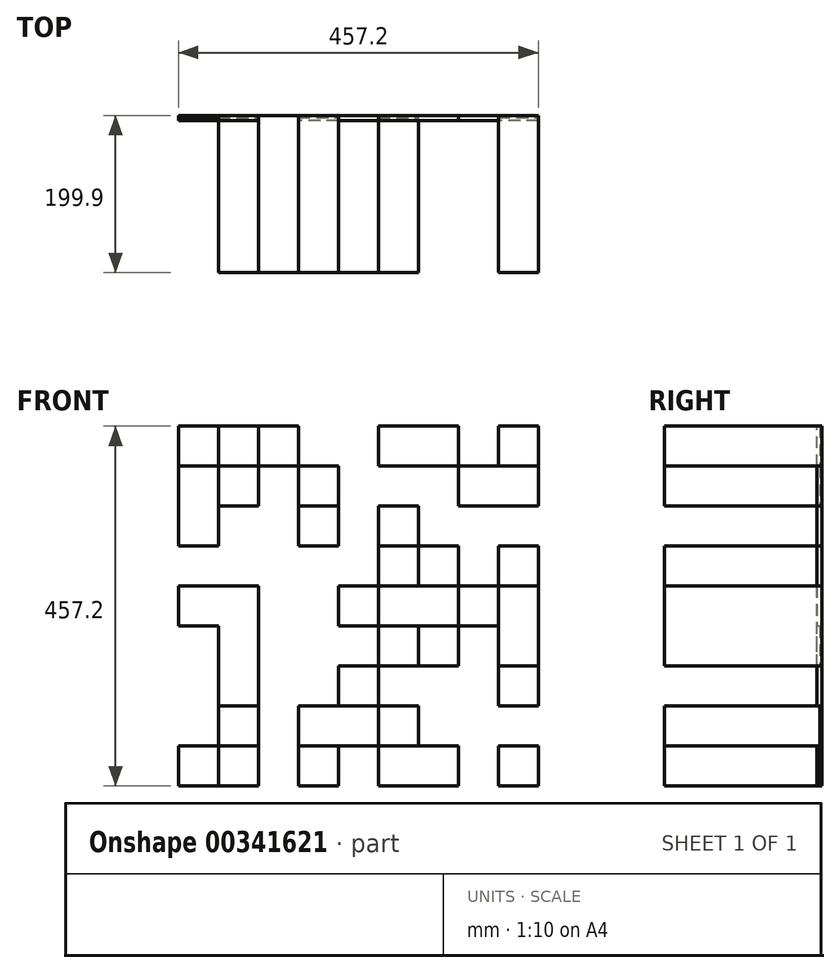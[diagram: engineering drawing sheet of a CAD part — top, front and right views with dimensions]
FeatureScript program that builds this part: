
annotation { "Feature Type Name" : "Feature", "Feature Type Description" : "" }
export const myFeature = defineFeature(function(context is Context, id is Id, definition is map)
    precondition{}
    {
        {
            var Q0;
            Q0=qCreatedBy(makeId("Front.planeOp"),FACE);
            var sketch = newSketch(context, id + "F0", { "sketchPlane" : qUnion([Q0])});
            skLineSegment(sketch, "E0.bottom", {"start": v(0, 0) * mm, "end": v(457.2, 0) * mm});
            skLineSegment(sketch, "E0.top", {"start": v(0, -457.2) * mm, "end": v(457.2, -457.2) * mm});
            skLineSegment(sketch, "E0.left", {"start": v(0, 0) * mm, "end": v(0, -457.2) * mm});
            skLineSegment(sketch, "E0.right", {"start": v(457.2, 0) * mm, "end": v(457.2, -457.2) * mm});
            skSolve(sketch);
        }
        {
            var Q0;
            Q0=qCreatedBy(makeId("Front.planeOp"),FACE);
            var sketch = newSketch(context, id + "F1", { "sketchPlane" : qUnion([Q0])});
            skLineSegment(sketch, "E1.bottom", {"start": v(0, 0) * mm, "end": v(50.8, 0) * mm});
            skLineSegment(sketch, "E1.top", {"start": v(0, -50.8) * mm, "end": v(50.8, -50.8) * mm});
            skLineSegment(sketch, "E1.left", {"start": v(0, 0) * mm, "end": v(0, -50.8) * mm});
            skLineSegment(sketch, "E1.right", {"start": v(50.8, 0) * mm, "end": v(50.8, -50.8) * mm});
            skLineSegment(sketch, "E2.bottom", {"start": v(50.8, 0) * mm, "end": v(101.6, 0) * mm});
            skLineSegment(sketch, "E2.top", {"start": v(50.8, -50.8) * mm, "end": v(101.6, -50.8) * mm});
            skLineSegment(sketch, "E2.right", {"start": v(101.6, 0) * mm, "end": v(101.6, -50.8) * mm});
            skLineSegment(sketch, "E3.bottom", {"start": v(101.6, 0) * mm, "end": v(152.4, 0) * mm});
            skLineSegment(sketch, "E3.top", {"start": v(101.6, -50.8) * mm, "end": v(152.4, -50.8) * mm});
            skLineSegment(sketch, "E3.right", {"start": v(152.4, 0) * mm, "end": v(152.4, -50.8) * mm});
            skLineSegment(sketch, "E4.bottom", {"start": v(152.4, 0) * mm, "end": v(203.2, 0) * mm});
            skLineSegment(sketch, "E4.top", {"start": v(152.4, -50.8) * mm, "end": v(203.2, -50.8) * mm});
            skLineSegment(sketch, "E4.right", {"start": v(203.2, 0) * mm, "end": v(203.2, -50.8) * mm});
            skLineSegment(sketch, "E5.bottom", {"start": v(203.2, 0) * mm, "end": v(254, 0) * mm});
            skLineSegment(sketch, "E5.top", {"start": v(203.2, -50.8) * mm, "end": v(254, -50.8) * mm});
            skLineSegment(sketch, "E5.right", {"start": v(254, 0) * mm, "end": v(254, -50.8) * mm});
            skLineSegment(sketch, "E6.bottom", {"start": v(254, 0) * mm, "end": v(304.8, 0) * mm});
            skLineSegment(sketch, "E6.top", {"start": v(254, -50.8) * mm, "end": v(304.8, -50.8) * mm});
            skLineSegment(sketch, "E6.right", {"start": v(304.8, 0) * mm, "end": v(304.8, -50.8) * mm});
            skLineSegment(sketch, "E7.bottom", {"start": v(304.8, 0) * mm, "end": v(355.6, 0) * mm});
            skLineSegment(sketch, "E7.top", {"start": v(304.8, -50.8) * mm, "end": v(355.6, -50.8) * mm});
            skLineSegment(sketch, "E7.right", {"start": v(355.6, 0) * mm, "end": v(355.6, -50.8) * mm});
            skLineSegment(sketch, "E8.bottom", {"start": v(355.6, 0) * mm, "end": v(406.4, 0) * mm});
            skLineSegment(sketch, "E8.top", {"start": v(355.6, -50.8) * mm, "end": v(406.4, -50.8) * mm});
            skLineSegment(sketch, "E8.right", {"start": v(406.4, 0) * mm, "end": v(406.4, -50.8) * mm});
            skLineSegment(sketch, "E9.bottom", {"start": v(406.4, 0) * mm, "end": v(457.2, 0) * mm});
            skLineSegment(sketch, "E9.top", {"start": v(406.4, -50.8) * mm, "end": v(457.2, -50.8) * mm});
            skLineSegment(sketch, "E9.right", {"start": v(457.2, 0) * mm, "end": v(457.2, -50.8) * mm});
            skLineSegment(sketch, "E10.top", {"start": v(0, -101.6) * mm, "end": v(50.8, -101.6) * mm});
            skLineSegment(sketch, "E10.left", {"start": v(0, -50.8) * mm, "end": v(0, -101.6) * mm});
            skLineSegment(sketch, "E10.right", {"start": v(50.8, -50.8) * mm, "end": v(50.8, -101.6) * mm});
            skLineSegment(sketch, "E11.top", {"start": v(50.8, -101.6) * mm, "end": v(101.6, -101.6) * mm});
            skLineSegment(sketch, "E11.right", {"start": v(101.6, -50.8) * mm, "end": v(101.6, -101.6) * mm});
            skLineSegment(sketch, "E12.top", {"start": v(50.8, -152.4) * mm, "end": v(101.6, -152.4) * mm});
            skLineSegment(sketch, "E12.left", {"start": v(50.8, -101.6) * mm, "end": v(50.8, -152.4) * mm});
            skLineSegment(sketch, "E12.right", {"start": v(101.6, -101.6) * mm, "end": v(101.6, -152.4) * mm});
            skLineSegment(sketch, "E13.bottom", {"start": v(101.6, -101.6) * mm, "end": v(152.4, -101.6) * mm});
            skLineSegment(sketch, "E13.top", {"start": v(101.6, -152.4) * mm, "end": v(152.4, -152.4) * mm});
            skLineSegment(sketch, "E13.right", {"start": v(152.4, -101.6) * mm, "end": v(152.4, -152.4) * mm});
            skLineSegment(sketch, "E14.top", {"start": v(304.8, -101.6) * mm, "end": v(355.6, -101.6) * mm});
            skLineSegment(sketch, "E14.left", {"start": v(304.8, -50.8) * mm, "end": v(304.8, -101.6) * mm});
            skLineSegment(sketch, "E14.right", {"start": v(355.6, -50.8) * mm, "end": v(355.6, -101.6) * mm});
            skLineSegment(sketch, "E15.top", {"start": v(0, -152.4) * mm, "end": v(50.8, -152.4) * mm});
            skLineSegment(sketch, "E15.left", {"start": v(0, -101.6) * mm, "end": v(0, -152.4) * mm});
            skLineSegment(sketch, "E16.top", {"start": v(406.4, -101.6) * mm, "end": v(457.2, -101.6) * mm});
            skLineSegment(sketch, "E16.left", {"start": v(406.4, -50.8) * mm, "end": v(406.4, -101.6) * mm});
            skLineSegment(sketch, "E16.right", {"start": v(457.2, -50.8) * mm, "end": v(457.2, -101.6) * mm});
            skLineSegment(sketch, "E17.top", {"start": v(355.6, -101.6) * mm, "end": v(406.4, -101.6) * mm});
            skLineSegment(sketch, "E18.top", {"start": v(254, -101.6) * mm, "end": v(304.8, -101.6) * mm});
            skLineSegment(sketch, "E18.left", {"start": v(254, -50.8) * mm, "end": v(254, -101.6) * mm});
            skLineSegment(sketch, "E19.top", {"start": v(152.4, -101.6) * mm, "end": v(203.2, -101.6) * mm});
            skLineSegment(sketch, "E19.left", {"start": v(152.4, -50.8) * mm, "end": v(152.4, -101.6) * mm});
            skLineSegment(sketch, "E19.right", {"start": v(203.2, -50.8) * mm, "end": v(203.2, -101.6) * mm});
            skLineSegment(sketch, "E20.top", {"start": v(203.2, -101.6) * mm, "end": v(254, -101.6) * mm});
            skLineSegment(sketch, "E21.top", {"start": v(0, -203.2) * mm, "end": v(50.8, -203.2) * mm});
            skLineSegment(sketch, "E21.left", {"start": v(0, -152.4) * mm, "end": v(0, -203.2) * mm});
            skLineSegment(sketch, "E21.right", {"start": v(50.8, -152.4) * mm, "end": v(50.8, -203.2) * mm});
            skLineSegment(sketch, "E22.top", {"start": v(50.8, -203.2) * mm, "end": v(101.6, -203.2) * mm});
            skLineSegment(sketch, "E22.right", {"start": v(101.6, -152.4) * mm, "end": v(101.6, -203.2) * mm});
            skLineSegment(sketch, "E23.bottom", {"start": v(152.4, -152.4) * mm, "end": v(203.2, -152.4) * mm});
            skLineSegment(sketch, "E23.top", {"start": v(152.4, -203.2) * mm, "end": v(203.2, -203.2) * mm});
            skLineSegment(sketch, "E23.left", {"start": v(152.4, -152.4) * mm, "end": v(152.4, -203.2) * mm});
            skLineSegment(sketch, "E23.right", {"start": v(203.2, -152.4) * mm, "end": v(203.2, -203.2) * mm});
            skLineSegment(sketch, "E24.top", {"start": v(304.8, -152.4) * mm, "end": v(355.6, -152.4) * mm});
            skLineSegment(sketch, "E24.left", {"start": v(304.8, -101.6) * mm, "end": v(304.8, -152.4) * mm});
            skLineSegment(sketch, "E24.right", {"start": v(355.6, -101.6) * mm, "end": v(355.6, -152.4) * mm});
            skLineSegment(sketch, "E25.top", {"start": v(406.4, -152.4) * mm, "end": v(457.2, -152.4) * mm});
            skLineSegment(sketch, "E25.left", {"start": v(406.4, -101.6) * mm, "end": v(406.4, -152.4) * mm});
            skLineSegment(sketch, "E25.right", {"start": v(457.2, -101.6) * mm, "end": v(457.2, -152.4) * mm});
            skLineSegment(sketch, "E26.top", {"start": v(101.6, -203.2) * mm, "end": v(152.4, -203.2) * mm});
            skLineSegment(sketch, "E27.bottom", {"start": v(203.2, -152.4) * mm, "end": v(254, -152.4) * mm});
            skLineSegment(sketch, "E27.top", {"start": v(203.2, -203.2) * mm, "end": v(254, -203.2) * mm});
            skLineSegment(sketch, "E27.right", {"start": v(254, -152.4) * mm, "end": v(254, -203.2) * mm});
            skLineSegment(sketch, "E28.bottom", {"start": v(254, -152.4) * mm, "end": v(304.8, -152.4) * mm});
            skLineSegment(sketch, "E28.top", {"start": v(254, -203.2) * mm, "end": v(304.8, -203.2) * mm});
            skLineSegment(sketch, "E28.right", {"start": v(304.8, -152.4) * mm, "end": v(304.8, -203.2) * mm});
            skLineSegment(sketch, "E29.left", {"start": v(254, -101.6) * mm, "end": v(254, -152.4) * mm});
            skLineSegment(sketch, "E30.top", {"start": v(355.6, -152.4) * mm, "end": v(406.4, -152.4) * mm});
            skLineSegment(sketch, "E31.left", {"start": v(203.2, -101.6) * mm, "end": v(203.2, -152.4) * mm});
            skLineSegment(sketch, "E32.bottom", {"start": v(304.8, -203.2) * mm, "end": v(355.6, -203.2) * mm});
            skLineSegment(sketch, "E32.top", {"start": v(304.8, -254) * mm, "end": v(355.6, -254) * mm});
            skLineSegment(sketch, "E32.left", {"start": v(304.8, -203.2) * mm, "end": v(304.8, -254) * mm});
            skLineSegment(sketch, "E32.right", {"start": v(355.6, -203.2) * mm, "end": v(355.6, -254) * mm});
            skLineSegment(sketch, "E33.top", {"start": v(203.2, -254) * mm, "end": v(254, -254) * mm});
            skLineSegment(sketch, "E33.left", {"start": v(203.2, -203.2) * mm, "end": v(203.2, -254) * mm});
            skLineSegment(sketch, "E33.right", {"start": v(254, -203.2) * mm, "end": v(254, -254) * mm});
            skLineSegment(sketch, "E34.bottom", {"start": v(355.6, -203.2) * mm, "end": v(406.4, -203.2) * mm});
            skLineSegment(sketch, "E34.top", {"start": v(355.6, -254) * mm, "end": v(406.4, -254) * mm});
            skLineSegment(sketch, "E34.right", {"start": v(406.4, -203.2) * mm, "end": v(406.4, -254) * mm});
            skLineSegment(sketch, "E35.top", {"start": v(101.6, -254) * mm, "end": v(152.4, -254) * mm});
            skLineSegment(sketch, "E35.left", {"start": v(101.6, -203.2) * mm, "end": v(101.6, -254) * mm});
            skLineSegment(sketch, "E35.right", {"start": v(152.4, -203.2) * mm, "end": v(152.4, -254) * mm});
            skLineSegment(sketch, "E36.top", {"start": v(152.4, -254) * mm, "end": v(203.2, -254) * mm});
            skLineSegment(sketch, "E37.top", {"start": v(254, -254) * mm, "end": v(304.8, -254) * mm});
            skLineSegment(sketch, "E38.left", {"start": v(355.6, -152.4) * mm, "end": v(355.6, -203.2) * mm});
            skLineSegment(sketch, "E38.right", {"start": v(406.4, -152.4) * mm, "end": v(406.4, -203.2) * mm});
            skLineSegment(sketch, "E39.top", {"start": v(0, -254) * mm, "end": v(50.8, -254) * mm});
            skLineSegment(sketch, "E39.left", {"start": v(0, -203.2) * mm, "end": v(0, -254) * mm});
            skLineSegment(sketch, "E39.right", {"start": v(50.8, -203.2) * mm, "end": v(50.8, -254) * mm});
            skLineSegment(sketch, "E40.top", {"start": v(50.8, -254) * mm, "end": v(101.6, -254) * mm});
            skLineSegment(sketch, "E41.top", {"start": v(406.4, -203.2) * mm, "end": v(457.2, -203.2) * mm});
            skLineSegment(sketch, "E41.right", {"start": v(457.2, -152.4) * mm, "end": v(457.2, -203.2) * mm});
            skLineSegment(sketch, "E42.top", {"start": v(0, -304.8) * mm, "end": v(50.8, -304.8) * mm});
            skLineSegment(sketch, "E42.left", {"start": v(0, -254) * mm, "end": v(0, -304.8) * mm});
            skLineSegment(sketch, "E42.right", {"start": v(50.8, -254) * mm, "end": v(50.8, -304.8) * mm});
            skLineSegment(sketch, "E43.top", {"start": v(355.6, -304.8) * mm, "end": v(406.4, -304.8) * mm});
            skLineSegment(sketch, "E43.left", {"start": v(355.6, -254) * mm, "end": v(355.6, -304.8) * mm});
            skLineSegment(sketch, "E43.right", {"start": v(406.4, -254) * mm, "end": v(406.4, -304.8) * mm});
            skLineSegment(sketch, "E44.top", {"start": v(355.6, -355.6) * mm, "end": v(406.4, -355.6) * mm});
            skLineSegment(sketch, "E44.left", {"start": v(355.6, -304.8) * mm, "end": v(355.6, -355.6) * mm});
            skLineSegment(sketch, "E44.right", {"start": v(406.4, -304.8) * mm, "end": v(406.4, -355.6) * mm});
            skLineSegment(sketch, "E45.top", {"start": v(0, -355.6) * mm, "end": v(50.8, -355.6) * mm});
            skLineSegment(sketch, "E45.left", {"start": v(0, -304.8) * mm, "end": v(0, -355.6) * mm});
            skLineSegment(sketch, "E45.right", {"start": v(50.8, -304.8) * mm, "end": v(50.8, -355.6) * mm});
            skLineSegment(sketch, "E46.bottom", {"start": v(101.6, -304.8) * mm, "end": v(152.4, -304.8) * mm});
            skLineSegment(sketch, "E46.top", {"start": v(101.6, -355.6) * mm, "end": v(152.4, -355.6) * mm});
            skLineSegment(sketch, "E46.left", {"start": v(101.6, -304.8) * mm, "end": v(101.6, -355.6) * mm});
            skLineSegment(sketch, "E46.right", {"start": v(152.4, -304.8) * mm, "end": v(152.4, -355.6) * mm});
            skLineSegment(sketch, "E47.top", {"start": v(101.6, -406.4) * mm, "end": v(152.4, -406.4) * mm});
            skLineSegment(sketch, "E47.left", {"start": v(101.6, -355.6) * mm, "end": v(101.6, -406.4) * mm});
            skLineSegment(sketch, "E47.right", {"start": v(152.4, -355.6) * mm, "end": v(152.4, -406.4) * mm});
            skLineSegment(sketch, "E48.top", {"start": v(406.4, -254) * mm, "end": v(457.2, -254) * mm});
            skLineSegment(sketch, "E48.right", {"start": v(457.2, -203.2) * mm, "end": v(457.2, -254) * mm});
            skLineSegment(sketch, "E49.left", {"start": v(101.6, -254) * mm, "end": v(101.6, -304.8) * mm});
            skLineSegment(sketch, "E49.right", {"start": v(152.4, -254) * mm, "end": v(152.4, -304.8) * mm});
            skLineSegment(sketch, "E50.top", {"start": v(203.2, -304.8) * mm, "end": v(254, -304.8) * mm});
            skLineSegment(sketch, "E50.left", {"start": v(203.2, -254) * mm, "end": v(203.2, -304.8) * mm});
            skLineSegment(sketch, "E50.right", {"start": v(254, -254) * mm, "end": v(254, -304.8) * mm});
            skLineSegment(sketch, "E51.bottom", {"start": v(304.8, -304.8) * mm, "end": v(355.6, -304.8) * mm});
            skLineSegment(sketch, "E51.top", {"start": v(304.8, -355.6) * mm, "end": v(355.6, -355.6) * mm});
            skLineSegment(sketch, "E51.left", {"start": v(304.8, -304.8) * mm, "end": v(304.8, -355.6) * mm});
            skLineSegment(sketch, "E52.top", {"start": v(355.6, -406.4) * mm, "end": v(406.4, -406.4) * mm});
            skLineSegment(sketch, "E52.left", {"start": v(355.6, -355.6) * mm, "end": v(355.6, -406.4) * mm});
            skLineSegment(sketch, "E52.right", {"start": v(406.4, -355.6) * mm, "end": v(406.4, -406.4) * mm});
            skLineSegment(sketch, "E53.top", {"start": v(0, -406.4) * mm, "end": v(50.8, -406.4) * mm});
            skLineSegment(sketch, "E53.left", {"start": v(0, -355.6) * mm, "end": v(0, -406.4) * mm});
            skLineSegment(sketch, "E53.right", {"start": v(50.8, -355.6) * mm, "end": v(50.8, -406.4) * mm});
            skLineSegment(sketch, "E54.bottom", {"start": v(406.4, -304.8) * mm, "end": v(457.2, -304.8) * mm});
            skLineSegment(sketch, "E54.top", {"start": v(406.4, -355.6) * mm, "end": v(457.2, -355.6) * mm});
            skLineSegment(sketch, "E54.right", {"start": v(457.2, -304.8) * mm, "end": v(457.2, -355.6) * mm});
            skLineSegment(sketch, "E55.bottom", {"start": v(50.8, -304.8) * mm, "end": v(101.6, -304.8) * mm});
            skLineSegment(sketch, "E55.top", {"start": v(50.8, -355.6) * mm, "end": v(101.6, -355.6) * mm});
            skLineSegment(sketch, "E56.top", {"start": v(50.8, -406.4) * mm, "end": v(101.6, -406.4) * mm});
            skLineSegment(sketch, "E57.bottom", {"start": v(254, -355.6) * mm, "end": v(304.8, -355.6) * mm});
            skLineSegment(sketch, "E57.top", {"start": v(254, -406.4) * mm, "end": v(304.8, -406.4) * mm});
            skLineSegment(sketch, "E57.left", {"start": v(254, -355.6) * mm, "end": v(254, -406.4) * mm});
            skLineSegment(sketch, "E57.right", {"start": v(304.8, -355.6) * mm, "end": v(304.8, -406.4) * mm});
            skLineSegment(sketch, "E58.top", {"start": v(152.4, -304.8) * mm, "end": v(203.2, -304.8) * mm});
            skLineSegment(sketch, "E59.bottom", {"start": v(254, -304.8) * mm, "end": v(304.8, -304.8) * mm});
            skLineSegment(sketch, "E59.left", {"start": v(254, -304.8) * mm, "end": v(254, -355.6) * mm});
            skLineSegment(sketch, "E60.left", {"start": v(304.8, -254) * mm, "end": v(304.8, -304.8) * mm});
            skLineSegment(sketch, "E61.top", {"start": v(203.2, -355.6) * mm, "end": v(254, -355.6) * mm});
            skLineSegment(sketch, "E61.left", {"start": v(203.2, -304.8) * mm, "end": v(203.2, -355.6) * mm});
            skLineSegment(sketch, "E62.top", {"start": v(152.4, -355.6) * mm, "end": v(203.2, -355.6) * mm});
            skLineSegment(sketch, "E63.top", {"start": v(304.8, -406.4) * mm, "end": v(355.6, -406.4) * mm});
            skLineSegment(sketch, "E64.bottom", {"start": v(203.2, -406.4) * mm, "end": v(254, -406.4) * mm});
            skLineSegment(sketch, "E64.top", {"start": v(203.2, -457.2) * mm, "end": v(254, -457.2) * mm});
            skLineSegment(sketch, "E64.left", {"start": v(203.2, -406.4) * mm, "end": v(203.2, -457.2) * mm});
            skLineSegment(sketch, "E64.right", {"start": v(254, -406.4) * mm, "end": v(254, -457.2) * mm});
            skLineSegment(sketch, "E65.top", {"start": v(355.6, -457.2) * mm, "end": v(406.4, -457.2) * mm});
            skLineSegment(sketch, "E65.left", {"start": v(355.6, -406.4) * mm, "end": v(355.6, -457.2) * mm});
            skLineSegment(sketch, "E65.right", {"start": v(406.4, -406.4) * mm, "end": v(406.4, -457.2) * mm});
            skLineSegment(sketch, "E66.top", {"start": v(50.8, -457.2) * mm, "end": v(101.6, -457.2) * mm});
            skLineSegment(sketch, "E66.left", {"start": v(50.8, -406.4) * mm, "end": v(50.8, -457.2) * mm});
            skLineSegment(sketch, "E66.right", {"start": v(101.6, -406.4) * mm, "end": v(101.6, -457.2) * mm});
            skLineSegment(sketch, "E67.top", {"start": v(152.4, -406.4) * mm, "end": v(203.2, -406.4) * mm});
            skLineSegment(sketch, "E67.right", {"start": v(203.2, -355.6) * mm, "end": v(203.2, -406.4) * mm});
            skLineSegment(sketch, "E68.bottom", {"start": v(406.4, -406.4) * mm, "end": v(457.2, -406.4) * mm});
            skLineSegment(sketch, "E68.top", {"start": v(406.4, -457.2) * mm, "end": v(457.2, -457.2) * mm});
            skLineSegment(sketch, "E68.right", {"start": v(457.2, -406.4) * mm, "end": v(457.2, -457.2) * mm});
            skLineSegment(sketch, "E69.top", {"start": v(304.8, -457.2) * mm, "end": v(355.6, -457.2) * mm});
            skLineSegment(sketch, "E69.left", {"start": v(304.8, -406.4) * mm, "end": v(304.8, -457.2) * mm});
            skLineSegment(sketch, "E70.top", {"start": v(101.6, -457.2) * mm, "end": v(152.4, -457.2) * mm});
            skLineSegment(sketch, "E70.right", {"start": v(152.4, -406.4) * mm, "end": v(152.4, -457.2) * mm});
            skLineSegment(sketch, "E71.right", {"start": v(457.2, -355.6) * mm, "end": v(457.2, -406.4) * mm});
            skLineSegment(sketch, "E72.right", {"start": v(457.2, -254) * mm, "end": v(457.2, -304.8) * mm});
            skLineSegment(sketch, "E73.top", {"start": v(152.4, -457.2) * mm, "end": v(203.2, -457.2) * mm});
            skLineSegment(sketch, "E74.top", {"start": v(0, -457.2) * mm, "end": v(50.8, -457.2) * mm});
            skLineSegment(sketch, "E74.left", {"start": v(0, -406.4) * mm, "end": v(0, -457.2) * mm});
            skLineSegment(sketch, "E75.top", {"start": v(254, -457.2) * mm, "end": v(304.8, -457.2) * mm});
            skSolve(sketch);
        }
        {
            var Q0;
            Q0 = qSketchRegion(id + "F0", true);
            extrude(context, id + "F2", {"entities" : qUnion([Q0]), "depth" : 6.35 * mm});
        }
        {
            var Q0;
            Q0=makeQuery(id+"F1.imprint","IMPRINT",FACE,{"disambiguationData":[TD([[makeQuery(id+"F1.imprint","IMPRINT",EDGE,{"derivedFrom":sQuery(id+"F1.wireOp",EDGE,"E4.bottom")}),-1.0]])]});
            var Q1;
            Q1=makeQuery(id+"F1.imprint","IMPRINT",FACE,{"disambiguationData":[TD([[makeQuery(id+"F1.imprint","IMPRINT",EDGE,{"derivedFrom":sQuery(id+"F1.wireOp",EDGE,"E8.bottom")}),-1.0]])]});
            var Q2;
            Q2=makeQuery(id+"F1.imprint","IMPRINT",FACE,{"disambiguationData":[TD([[makeQuery(id+"F1.imprint","IMPRINT",EDGE,{"derivedFrom":sQuery(id+"F1.wireOp",EDGE,"E3.top")}),-1.0]])]});
            var Q3;
            Q3=makeQuery(id+"F1.imprint","IMPRINT",FACE,{"disambiguationData":[TD([[makeQuery(id+"F1.imprint","IMPRINT",EDGE,{"derivedFrom":sQuery(id+"F1.wireOp",EDGE,"E7.top")}),-1.0]])]});
            var Q4;
            Q4=makeQuery(id+"F1.imprint","IMPRINT",FACE,{"disambiguationData":[TD([[makeQuery(id+"F1.imprint","IMPRINT",EDGE,{"derivedFrom":sQuery(id+"F1.wireOp",EDGE,"E6.top")}),-1.0]])]});
            var Q5;
            Q5=makeQuery(id+"F1.imprint","IMPRINT",FACE,{"disambiguationData":[TD([[makeQuery(id+"F1.imprint","IMPRINT",EDGE,{"derivedFrom":sQuery(id+"F1.wireOp",EDGE,"E11.top")}),-1.0]])]});
            var Q6;
            Q6=makeQuery(id+"F1.imprint","IMPRINT",FACE,{"disambiguationData":[TD([[makeQuery(id+"F1.imprint","IMPRINT",EDGE,{"derivedFrom":sQuery(id+"F1.wireOp",EDGE,"E13.bottom")}),-1.0]])]});
            var Q7;
            Q7=makeQuery(id+"F1.imprint","IMPRINT",FACE,{"disambiguationData":[TD([[makeQuery(id+"F1.imprint","IMPRINT",EDGE,{"derivedFrom":sQuery(id+"F1.wireOp",EDGE,"E20.top")}),-1.0]])]});
            var Q8;
            Q8=makeQuery(id+"F1.imprint","IMPRINT",FACE,{"disambiguationData":[TD([[makeQuery(id+"F1.imprint","IMPRINT",EDGE,{"derivedFrom":sQuery(id+"F1.wireOp",EDGE,"E16.top")}),-1.0]])]});
            var Q9;
            Q9=makeQuery(id+"F1.imprint","IMPRINT",FACE,{"disambiguationData":[TD([[makeQuery(id+"F1.imprint","IMPRINT",EDGE,{"derivedFrom":sQuery(id+"F1.wireOp",EDGE,"E26.top")}),-1.0]])]});
            var Q10;
            Q10=makeQuery(id+"F1.imprint","IMPRINT",FACE,{"disambiguationData":[TD([[makeQuery(id+"F1.imprint","IMPRINT",EDGE,{"derivedFrom":sQuery(id+"F1.wireOp",EDGE,"E23.top")}),-1.0]])]});
            var Q11;
            Q11=makeQuery(id+"F1.imprint","IMPRINT",FACE,{"disambiguationData":[TD([[makeQuery(id+"F1.imprint","IMPRINT",EDGE,{"derivedFrom":sQuery(id+"F1.wireOp",EDGE,"E28.top")}),-1.0]])]});
            var Q12;
            Q12=makeQuery(id+"F1.imprint","IMPRINT",FACE,{"disambiguationData":[TD([[makeQuery(id+"F1.imprint","IMPRINT",EDGE,{"derivedFrom":sQuery(id+"F1.wireOp",EDGE,"E32.bottom")}),-1.0]])]});
            var Q13;
            Q13=makeQuery(id+"F1.imprint","IMPRINT",FACE,{"disambiguationData":[TD([[makeQuery(id+"F1.imprint","IMPRINT",EDGE,{"derivedFrom":sQuery(id+"F1.wireOp",EDGE,"E32.bottom")}),-1.0]])]});
            var Q14;
            Q14=makeQuery(id+"F1.imprint","IMPRINT",FACE,{"disambiguationData":[TD([[makeQuery(id+"F1.imprint","IMPRINT",EDGE,{"derivedFrom":sQuery(id+"F1.wireOp",EDGE,"E32.bottom")}),-1.0]])]});
            var Q15;
            Q15=makeQuery(id+"F1.imprint","IMPRINT",FACE,{"disambiguationData":[TD([[makeQuery(id+"F1.imprint","IMPRINT",EDGE,{"derivedFrom":sQuery(id+"F1.wireOp",EDGE,"E36.top")}),-1.0]])]});
            var Q16;
            Q16=makeQuery(id+"F1.imprint","IMPRINT",FACE,{"disambiguationData":[TD([[makeQuery(id+"F1.imprint","IMPRINT",EDGE,{"derivedFrom":sQuery(id+"F1.wireOp",EDGE,"E58.top")}),-1.0]])]});
            var Q17;
            Q17=makeQuery(id+"F1.imprint","IMPRINT",FACE,{"disambiguationData":[TD([[makeQuery(id+"F1.imprint","IMPRINT",EDGE,{"derivedFrom":sQuery(id+"F1.wireOp",EDGE,"E51.top")}),-1.0]])]});
            var Q18;
            Q18=makeQuery(id+"F1.imprint","IMPRINT",FACE,{"disambiguationData":[TD([[makeQuery(id+"F1.imprint","IMPRINT",EDGE,{"derivedFrom":sQuery(id+"F1.wireOp",EDGE,"E59.bottom")}),-1.0]])]});
            var Q19;
            Q19=makeQuery(id+"F1.imprint","IMPRINT",FACE,{"disambiguationData":[TD([[makeQuery(id+"F1.imprint","IMPRINT",EDGE,{"derivedFrom":sQuery(id+"F1.wireOp",EDGE,"E47.top")}),-1.0]])]});
            var Q20;
            Q20=makeQuery(id+"F1.imprint","IMPRINT",FACE,{"disambiguationData":[TD([[makeQuery(id+"F1.imprint","IMPRINT",EDGE,{"derivedFrom":sQuery(id+"F1.wireOp",EDGE,"E54.top")}),-1.0]])]});
            var Q21;
            Q21=makeQuery(id+"F1.imprint","IMPRINT",FACE,{"disambiguationData":[TD([[makeQuery(id+"F1.imprint","IMPRINT",EDGE,{"derivedFrom":sQuery(id+"F1.wireOp",EDGE,"E52.top")}),-1.0]])]});
            var Q22;
            Q22=makeQuery(id+"F1.imprint","IMPRINT",FACE,{"disambiguationData":[TD([[makeQuery(id+"F1.imprint","IMPRINT",EDGE,{"derivedFrom":sQuery(id+"F1.wireOp",EDGE,"E64.bottom")}),-1.0]])]});
            extrude(context, id + "F3", {"entities" : qUnion([Q0, Q1, Q2, Q3, Q4, Q5, Q6, Q7, Q8, Q9, Q10, Q11, Q12, Q13, Q14, Q15, Q16, Q17, Q18, Q19, Q20, Q21, Q22]), "depth" : 50.04 * mm});
        }
        {
            var Q0;
            Q0=makeQuery(id+"F1.imprint","IMPRINT",FACE,{"disambiguationData":[TD([[makeQuery(id+"F1.imprint","IMPRINT",EDGE,{"derivedFrom":sQuery(id+"F1.wireOp",EDGE,"E5.bottom")}),-1.0]])]});
            var Q1;
            Q1=makeQuery(id+"F1.imprint","IMPRINT",FACE,{"disambiguationData":[TD([[makeQuery(id+"F1.imprint","IMPRINT",EDGE,{"derivedFrom":sQuery(id+"F1.wireOp",EDGE,"E5.top")}),-1.0]])]});
            var Q2;
            Q2=makeQuery(id+"F1.imprint","IMPRINT",FACE,{"disambiguationData":[TD([[makeQuery(id+"F1.imprint","IMPRINT",EDGE,{"derivedFrom":sQuery(id+"F1.wireOp",EDGE,"E17.top")}),-1.0]])]});
            var Q3;
            Q3=makeQuery(id+"F1.imprint","IMPRINT",FACE,{"disambiguationData":[TD([[makeQuery(id+"F1.imprint","IMPRINT",EDGE,{"derivedFrom":sQuery(id+"F1.wireOp",EDGE,"E14.top")}),-1.0]])]});
            var Q4;
            Q4=makeQuery(id+"F1.imprint","IMPRINT",FACE,{"disambiguationData":[TD([[makeQuery(id+"F1.imprint","IMPRINT",EDGE,{"derivedFrom":sQuery(id+"F1.wireOp",EDGE,"E15.top")}),-1.0]])]});
            var Q5;
            Q5=makeQuery(id+"F1.imprint","IMPRINT",FACE,{"disambiguationData":[TD([[makeQuery(id+"F1.imprint","IMPRINT",EDGE,{"derivedFrom":sQuery(id+"F1.wireOp",EDGE,"E12.top")}),-1.0]])]});
            var Q6;
            Q6=makeQuery(id+"F1.imprint","IMPRINT",FACE,{"disambiguationData":[TD([[makeQuery(id+"F1.imprint","IMPRINT",EDGE,{"derivedFrom":sQuery(id+"F1.wireOp",EDGE,"E13.top")}),-1.0]])]});
            var Q7;
            Q7=makeQuery(id+"F1.imprint","IMPRINT",FACE,{"disambiguationData":[TD([[makeQuery(id+"F1.imprint","IMPRINT",EDGE,{"derivedFrom":sQuery(id+"F1.wireOp",EDGE,"2b75bbf8-d74c-421c-a9b6-6d7b0d96c7b7.bottom")}),-1.0]])]});
            var Q8;
            Q8=makeQuery(id+"F1.imprint","IMPRINT",FACE,{"disambiguationData":[TD([[makeQuery(id+"F1.imprint","IMPRINT",EDGE,{"derivedFrom":sQuery(id+"F1.wireOp",EDGE,"E23.bottom")}),-1.0]])]});
            var Q9;
            Q9=makeQuery(id+"F1.imprint","IMPRINT",FACE,{"disambiguationData":[TD([[makeQuery(id+"F1.imprint","IMPRINT",EDGE,{"derivedFrom":sQuery(id+"F1.wireOp",EDGE,"E30.top")}),-1.0]])]});
            var Q10;
            Q10=makeQuery(id+"F1.imprint","IMPRINT",FACE,{"disambiguationData":[TD([[makeQuery(id+"F1.imprint","IMPRINT",EDGE,{"derivedFrom":sQuery(id+"F1.wireOp",EDGE,"E39.top")}),-1.0]])]});
            var Q11;
            Q11=makeQuery(id+"F1.imprint","IMPRINT",FACE,{"disambiguationData":[TD([[makeQuery(id+"F1.imprint","IMPRINT",EDGE,{"derivedFrom":sQuery(id+"F1.wireOp",EDGE,"a57881f6-9dc0-412f-bbc8-27bb82300bed.bottom")}),-1.0]])]});
            var Q12;
            Q12=makeQuery(id+"F1.imprint","IMPRINT",FACE,{"disambiguationData":[TD([[makeQuery(id+"F1.imprint","IMPRINT",EDGE,{"derivedFrom":sQuery(id+"F1.wireOp",EDGE,"E35.top")}),-1.0]])]});
            var Q13;
            Q13=makeQuery(id+"F1.imprint","IMPRINT",FACE,{"disambiguationData":[TD([[makeQuery(id+"F1.imprint","IMPRINT",EDGE,{"derivedFrom":sQuery(id+"F1.wireOp",EDGE,"E33.top")}),-1.0]])]});
            var Q14;
            Q14=makeQuery(id+"F1.imprint","IMPRINT",FACE,{"disambiguationData":[TD([[makeQuery(id+"F1.imprint","IMPRINT",EDGE,{"derivedFrom":sQuery(id+"F1.wireOp",EDGE,"E34.top")}),-1.0]])]});
            var Q15;
            Q15=makeQuery(id+"F1.imprint","IMPRINT",FACE,{"disambiguationData":[TD([[makeQuery(id+"F1.imprint","IMPRINT",EDGE,{"derivedFrom":sQuery(id+"F1.wireOp",EDGE,"E43.top")}),-1.0]])]});
            var Q16;
            {var subQ1=sQuery(id+"F1.wireOp",EDGE,"E51.bottom");Q16=makeQuery(id+"F1.imprint","IMPRINT",FACE,{"disambiguationData":[TD([[makeQuery(id+"F1.imprint","IMPRINT",EDGE,{"derivedFrom":subQ1}),-1.0]])]});}
            var Q17;
            {var subQ0=sQuery(id+"F1.wireOp",EDGE,"E52.top");Q17=makeQuery(id+"F1.imprint","IMPRINT",FACE,{"disambiguationData":[TD([[makeQuery(id+"F1.imprint","IMPRINT",EDGE,{"derivedFrom":subQ0}),1.0]])]});}
            var Q18;
            Q18=makeQuery(id+"F1.imprint","IMPRINT",FACE,{"disambiguationData":[TD([[makeQuery(id+"F1.imprint","IMPRINT",EDGE,{"derivedFrom":sQuery(id+"F1.wireOp",EDGE,"E45.top")}),-1.0]])]});
            var Q19;
            Q19=makeQuery(id+"F1.imprint","IMPRINT",FACE,{"disambiguationData":[TD([[makeQuery(id+"F1.imprint","IMPRINT",EDGE,{"derivedFrom":sQuery(id+"F1.wireOp",EDGE,"E42.top")}),-1.0]])]});
            var Q20;
            Q20=makeQuery(id+"F1.imprint","IMPRINT",FACE,{"disambiguationData":[TD([[makeQuery(id+"F1.imprint","IMPRINT",EDGE,{"derivedFrom":sQuery(id+"F1.wireOp",EDGE,"E46.bottom")}),-1.0]])]});
            var Q21;
            Q21=makeQuery(id+"F1.imprint","IMPRINT",FACE,{"disambiguationData":[TD([[makeQuery(id+"F1.imprint","IMPRINT",EDGE,{"derivedFrom":sQuery(id+"F1.wireOp",EDGE,"E46.top")}),-1.0]])]});
            var Q22;
            Q22=makeQuery(id+"F1.imprint","IMPRINT",FACE,{"disambiguationData":[TD([[makeQuery(id+"F1.imprint","IMPRINT",EDGE,{"derivedFrom":sQuery(id+"F1.wireOp",EDGE,"E46.bottom")}),-1.0]])]});
            var Q23;
            Q23=makeQuery(id+"F1.imprint","IMPRINT",FACE,{"disambiguationData":[TD([[makeQuery(id+"F1.imprint","IMPRINT",EDGE,{"derivedFrom":sQuery(id+"F1.wireOp",EDGE,"E46.top")}),-1.0]])]});
            extrude(context, id + "F4", {"entities" : qUnion([Q0, Q1, Q2, Q3, Q4, Q5, Q6, Q7, Q8, Q9, Q10, Q11, Q12, Q13, Q14, Q15, Q16, Q17, Q18, Q19, Q20, Q21, Q22, Q23]), "depth" : 100.08 * mm});
        }
        {
            var Q0;
            {var subQ4=sQuery(id+"F1.wireOp",EDGE,"E2.bottom");Q0=makeQuery(id+"F1.imprint","IMPRINT",FACE,{"disambiguationData":[TD([[makeQuery(id+"F1.imprint","IMPRINT",EDGE,{"derivedFrom":subQ4}),-1.0]])]});}
            var Q1;
            Q1=makeQuery(id+"F1.imprint","IMPRINT",FACE,{"disambiguationData":[TD([[makeQuery(id+"F1.imprint","IMPRINT",EDGE,{"derivedFrom":sQuery(id+"F1.wireOp",EDGE,"E6.bottom")}),-1.0]])]});
            var Q2;
            Q2=makeQuery(id+"F1.imprint","IMPRINT",FACE,{"disambiguationData":[TD([[makeQuery(id+"F1.imprint","IMPRINT",EDGE,{"derivedFrom":sQuery(id+"F1.wireOp",EDGE,"E7.bottom")}),-1.0]])]});
            var Q3;
            Q3=makeQuery(id+"F1.imprint","IMPRINT",FACE,{"disambiguationData":[TD([[makeQuery(id+"F1.imprint","IMPRINT",EDGE,{"derivedFrom":sQuery(id+"F1.wireOp",EDGE,"E1.top")}),-1.0]])]});
            var Q4;
            Q4=makeQuery(id+"F1.imprint","IMPRINT",FACE,{"disambiguationData":[TD([[makeQuery(id+"F1.imprint","IMPRINT",EDGE,{"derivedFrom":sQuery(id+"F1.wireOp",EDGE,"E9.top")}),-1.0]])]});
            var Q5;
            Q5=makeQuery(id+"F1.imprint","IMPRINT",FACE,{"disambiguationData":[TD([[makeQuery(id+"F1.imprint","IMPRINT",EDGE,{"derivedFrom":sQuery(id+"F1.wireOp",EDGE,"E8.top")}),-1.0]])]});
            var Q6;
            Q6=makeQuery(id+"F1.imprint","IMPRINT",FACE,{"disambiguationData":[TD([[makeQuery(id+"F1.imprint","IMPRINT",EDGE,{"derivedFrom":sQuery(id+"F1.wireOp",EDGE,"E10.top")}),-1.0]])]});
            var Q7;
            Q7=makeQuery(id+"F1.imprint","IMPRINT",FACE,{"disambiguationData":[TD([[makeQuery(id+"F1.imprint","IMPRINT",EDGE,{"derivedFrom":sQuery(id+"F1.wireOp",EDGE,"E19.top")}),-1.0]])]});
            var Q8;
            Q8=makeQuery(id+"F1.imprint","IMPRINT",FACE,{"disambiguationData":[TD([[makeQuery(id+"F1.imprint","IMPRINT",EDGE,{"derivedFrom":sQuery(id+"F1.wireOp",EDGE,"E18.top")}),-1.0]])]});
            var Q9;
            Q9=makeQuery(id+"F1.imprint","IMPRINT",FACE,{"disambiguationData":[TD([[makeQuery(id+"F1.imprint","IMPRINT",EDGE,{"derivedFrom":sQuery(id+"F1.wireOp",EDGE,"E21.top")}),-1.0]])]});
            var Q10;
            Q10=makeQuery(id+"F1.imprint","IMPRINT",FACE,{"disambiguationData":[TD([[makeQuery(id+"F1.imprint","IMPRINT",EDGE,{"derivedFrom":sQuery(id+"F1.wireOp",EDGE,"E22.top")}),-1.0]])]});
            var Q11;
            Q11=makeQuery(id+"F1.imprint","IMPRINT",FACE,{"disambiguationData":[TD([[makeQuery(id+"F1.imprint","IMPRINT",EDGE,{"derivedFrom":sQuery(id+"F1.wireOp",EDGE,"39fd1b97-4bb1-454f-9889-2505326d38ac.bottom")}),-1.0]])]});
            var Q12;
            Q12=makeQuery(id+"F1.imprint","IMPRINT",FACE,{"disambiguationData":[TD([[makeQuery(id+"F1.imprint","IMPRINT",EDGE,{"derivedFrom":sQuery(id+"F1.wireOp",EDGE,"E25.top")}),-1.0]])]});
            var Q13;
            Q13=makeQuery(id+"F1.imprint","IMPRINT",FACE,{"disambiguationData":[TD([[makeQuery(id+"F1.imprint","IMPRINT",EDGE,{"derivedFrom":sQuery(id+"F1.wireOp",EDGE,"E24.top")}),-1.0]])]});
            var Q14;
            Q14=makeQuery(id+"F1.imprint","IMPRINT",FACE,{"disambiguationData":[TD([[makeQuery(id+"F1.imprint","IMPRINT",EDGE,{"derivedFrom":sQuery(id+"F1.wireOp",EDGE,"E27.top")}),-1.0]])]});
            var Q15;
            Q15=makeQuery(id+"F1.imprint","IMPRINT",FACE,{"disambiguationData":[TD([[makeQuery(id+"F1.imprint","IMPRINT",EDGE,{"derivedFrom":sQuery(id+"F1.wireOp",EDGE,"E34.bottom")}),-1.0]])]});
            var Q16;
            Q16=makeQuery(id+"F1.imprint","IMPRINT",FACE,{"disambiguationData":[TD([[makeQuery(id+"F1.imprint","IMPRINT",EDGE,{"derivedFrom":sQuery(id+"F1.wireOp",EDGE,"E54.bottom")}),-1.0]])]});
            var Q17;
            Q17=makeQuery(id+"F1.imprint","IMPRINT",FACE,{"disambiguationData":[TD([[makeQuery(id+"F1.imprint","IMPRINT",EDGE,{"derivedFrom":sQuery(id+"F1.wireOp",EDGE,"E32.top")}),-1.0]])]});
            var Q18;
            Q18=makeQuery(id+"F1.imprint","IMPRINT",FACE,{"disambiguationData":[TD([[makeQuery(id+"F1.imprint","IMPRINT",EDGE,{"derivedFrom":sQuery(id+"F1.wireOp",EDGE,"E50.top")}),-1.0]])]});
            var Q19;
            Q19=makeQuery(id+"F1.imprint","IMPRINT",FACE,{"disambiguationData":[TD([[makeQuery(id+"F1.imprint","IMPRINT",EDGE,{"derivedFrom":sQuery(id+"F1.wireOp",EDGE,"E55.bottom")}),-1.0]])]});
            var Q20;
            Q20=makeQuery(id+"F1.imprint","IMPRINT",FACE,{"disambiguationData":[TD([[makeQuery(id+"F1.imprint","IMPRINT",EDGE,{"derivedFrom":sQuery(id+"F1.wireOp",EDGE,"E40.top")}),-1.0]])]});
            var Q21;
            Q21=makeQuery(id+"F1.imprint","IMPRINT",FACE,{"disambiguationData":[TD([[makeQuery(id+"F1.imprint","IMPRINT",EDGE,{"derivedFrom":sQuery(id+"F1.wireOp",EDGE,"E53.top")}),-1.0]])]});
            var Q22;
            Q22=makeQuery(id+"F1.imprint","IMPRINT",FACE,{"disambiguationData":[TD([[makeQuery(id+"F1.imprint","IMPRINT",EDGE,{"derivedFrom":sQuery(id+"F1.wireOp",EDGE,"E57.top")}),-1.0]])]});
            var Q23;
            Q23=makeQuery(id+"F1.imprint","IMPRINT",FACE,{"disambiguationData":[TD([[makeQuery(id+"F1.imprint","IMPRINT",EDGE,{"derivedFrom":sQuery(id+"F1.wireOp",EDGE,"E63.top")}),-1.0]])]});
            extrude(context, id + "F5", {"entities" : qUnion([Q0, Q1, Q2, Q3, Q4, Q5, Q6, Q7, Q8, Q9, Q10, Q11, Q12, Q13, Q14, Q15, Q16, Q17, Q18, Q19, Q20, Q21, Q22, Q23]), "operationType" : NewBodyOperationType.INTERSECT, "depth" : 149.86 * mm});
        }
        {
            var Q0;
            Q0=makeQuery(id+"F1.imprint","IMPRINT",FACE,{"disambiguationData":[TD([[makeQuery(id+"F1.imprint","IMPRINT",EDGE,{"derivedFrom":sQuery(id+"F1.wireOp",EDGE,"E3.bottom")}),-1.0]])]});
            var Q1;
            Q1=makeQuery(id+"F1.imprint","IMPRINT",FACE,{"disambiguationData":[TD([[makeQuery(id+"F1.imprint","IMPRINT",EDGE,{"derivedFrom":sQuery(id+"F1.wireOp",EDGE,"E9.bottom")}),-1.0]])]});
            var Q2;
            Q2=makeQuery(id+"F1.imprint","IMPRINT",FACE,{"disambiguationData":[TD([[makeQuery(id+"F1.imprint","IMPRINT",EDGE,{"derivedFrom":sQuery(id+"F1.wireOp",EDGE,"E4.top")}),-1.0]])]});
            var Q3;
            Q3=makeQuery(id+"F1.imprint","IMPRINT",FACE,{"disambiguationData":[TD([[makeQuery(id+"F1.imprint","IMPRINT",EDGE,{"derivedFrom":sQuery(id+"F1.wireOp",EDGE,"E28.bottom")}),-1.0]])]});
            var Q4;
            Q4=makeQuery(id+"F1.imprint","IMPRINT",FACE,{"disambiguationData":[TD([[makeQuery(id+"F1.imprint","IMPRINT",EDGE,{"derivedFrom":sQuery(id+"F1.wireOp",EDGE,"E41.top")}),-1.0]])]});
            var Q5;
            Q5=makeQuery(id+"F1.imprint","IMPRINT",FACE,{"disambiguationData":[TD([[makeQuery(id+"F1.imprint","IMPRINT",EDGE,{"derivedFrom":sQuery(id+"F1.wireOp",EDGE,"E56.top")}),-1.0]])]});
            var Q6;
            Q6=makeQuery(id+"F1.imprint","IMPRINT",FACE,{"disambiguationData":[TD([[makeQuery(id+"F1.imprint","IMPRINT",EDGE,{"derivedFrom":sQuery(id+"F1.wireOp",EDGE,"E48.top")}),-1.0]])]});
            var Q7;
            Q7=makeQuery(id+"F1.imprint","IMPRINT",FACE,{"disambiguationData":[TD([[makeQuery(id+"F1.imprint","IMPRINT",EDGE,{"derivedFrom":sQuery(id+"F1.wireOp",EDGE,"E62.top")}),-1.0]])]});
            var Q8;
            Q8=makeQuery(id+"F1.imprint","IMPRINT",FACE,{"disambiguationData":[TD([[makeQuery(id+"F1.imprint","IMPRINT",EDGE,{"derivedFrom":sQuery(id+"F1.wireOp",EDGE,"E61.top")}),-1.0]])]});
            extrude(context, id + "F6", {"entities" : qUnion([Q0, Q1, Q2, Q3, Q4, Q5, Q6, Q7, Q8]), "depth" : 199.9 * mm});
        }
        {
            var Q0;
            Q0=makeQuery(id+"F1.imprint","IMPRINT",FACE,{"disambiguationData":[TD([[makeQuery(id+"F1.imprint","IMPRINT",EDGE,{"derivedFrom":sQuery(id+"F1.wireOp",EDGE,"E1.bottom")}),-1.0]])]});
            var Q1;
            Q1=makeQuery(id+"F1.imprint","IMPRINT",FACE,{"disambiguationData":[TD([[makeQuery(id+"F1.imprint","IMPRINT",EDGE,{"derivedFrom":sQuery(id+"F1.wireOp",EDGE,"E2.top")}),-1.0]])]});
            var Q2;
            Q2=makeQuery(id+"F1.imprint","IMPRINT",FACE,{"disambiguationData":[TD([[makeQuery(id+"F1.imprint","IMPRINT",EDGE,{"derivedFrom":sQuery(id+"F1.wireOp",EDGE,"E37.top")}),-1.0]])]});
            var Q3;
            Q3=makeQuery(id+"F1.imprint","IMPRINT",FACE,{"disambiguationData":[TD([[makeQuery(id+"F1.imprint","IMPRINT",EDGE,{"derivedFrom":sQuery(id+"F1.wireOp",EDGE,"E55.top")}),-1.0]])]});
            var Q4;
            Q4=makeQuery(id+"F1.imprint","IMPRINT",FACE,{"disambiguationData":[TD([[makeQuery(id+"F1.imprint","IMPRINT",EDGE,{"derivedFrom":sQuery(id+"F1.wireOp",EDGE,"E57.bottom")}),-1.0]])]});
            var Q5;
            Q5=makeQuery(id+"F1.imprint","IMPRINT",FACE,{"disambiguationData":[TD([[makeQuery(id+"F1.imprint","IMPRINT",EDGE,{"derivedFrom":sQuery(id+"F1.wireOp",EDGE,"E68.bottom")}),-1.0]])]});
            var Q6;
            Q6=makeQuery(id+"F1.imprint","IMPRINT",FACE,{"disambiguationData":[TD([[makeQuery(id+"F1.imprint","IMPRINT",EDGE,{"derivedFrom":sQuery(id+"F1.wireOp",EDGE,"E67.top")}),-1.0]])]});
            extrude(context, id + "F7", {"entities" : qUnion([Q0, Q1, Q2, Q3, Q4, Q5, Q6]), "depth" : 2.54 * mm});
        }
    });
